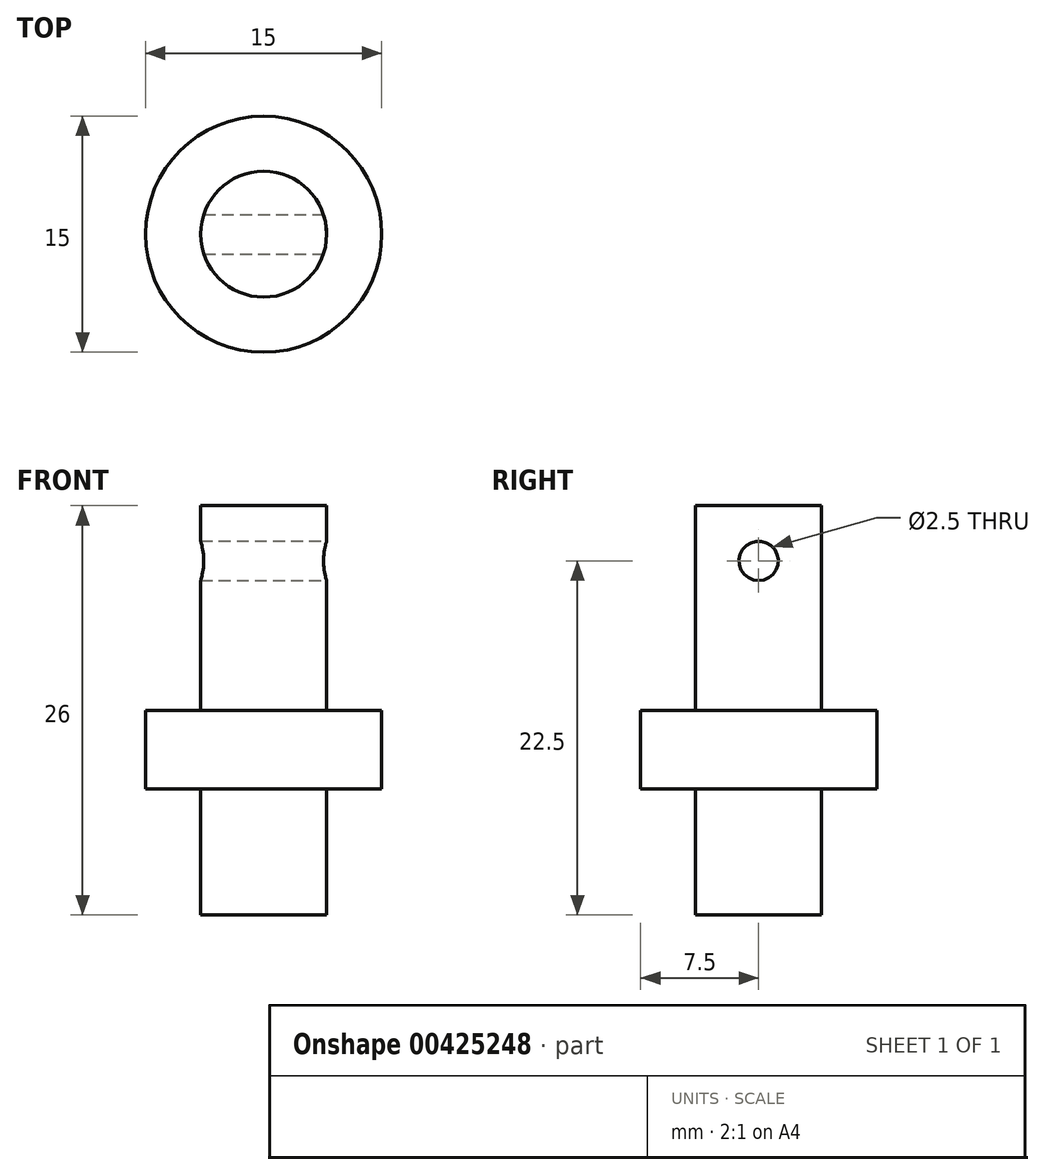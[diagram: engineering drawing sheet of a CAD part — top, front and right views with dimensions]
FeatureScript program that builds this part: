
annotation { "Feature Type Name" : "Feature", "Feature Type Description" : "" }
export const myFeature = defineFeature(function(context is Context, id is Id, definition is map)
    precondition{}
    {
        {
            var Q0;
            Q0=qCreatedBy(makeId("Top.planeOp"),FACE);
            var sketch = newSketch(context, id + "F0", { "sketchPlane" : qUnion([Q0])});
            skCircle(sketch, "E0", {"center": v(0, 0) * mm, "radius": 4 * mm});
            skSolve(sketch);
        }
        {
            var Q0;
            Q0 = qSketchRegion(id + "F0", true);
            extrude(context, id + "F1", {"entities" : qUnion([Q0]), "depth" : 26 * mm});
        }
        {
            var Q0;
            Q0=makeQuery(id+"F1.opExtrude","CAP_FACE",FACE,{"disambiguationData":[OSD([sQuery(id+"F0.wireOp",EDGE,"E0")])],"isStart":true});
            cPlane(context, id + "F2", {"entities" : qUnion([Q0]), "cplaneType" : CPlaneType.OFFSET, "offset" : 8 * mm, "oppositeDirection" : true, "width" : 150 * mm, "height" : 150 * mm});
        }
        {
            var Q0;
            Q0=qCreatedBy(id+"F2.planeOp",FACE);
            var sketch = newSketch(context, id + "F3", { "sketchPlane" : qUnion([Q0])});
            skCircle(sketch, "E1", {"center": v(0, 0) * mm, "radius": 7.5 * mm});
            skSolve(sketch);
        }
        {
            var Q0;
            Q0 = qSketchRegion(id + "F3", true);
            extrude(context, id + "F4", {"entities" : qUnion([Q0]), "operationType" : NewBodyOperationType.ADD, "oppositeDirection" : true, "depth" : 5 * mm});
        }
        {
            var Q0;
            Q0=qCreatedBy(makeId("Right.planeOp"),FACE);
            var sketch = newSketch(context, id + "F5", { "sketchPlane" : qUnion([Q0])});
            skCircle(sketch, "E2", {"center": v(0, 22.5) * mm, "radius": 1.25 * mm});
            skSolve(sketch);
        }
        {
            var Q0;
            Q0 = qSketchRegion(id + "F5", true);
            extrude(context, id + "F6", {"entities" : qUnion([Q0]), "operationType" : NewBodyOperationType.REMOVE, "endBound" : BoundingType.SYMMETRIC, "oppositeDirection" : true, "depth" : 25 * mm});
        }
    });
